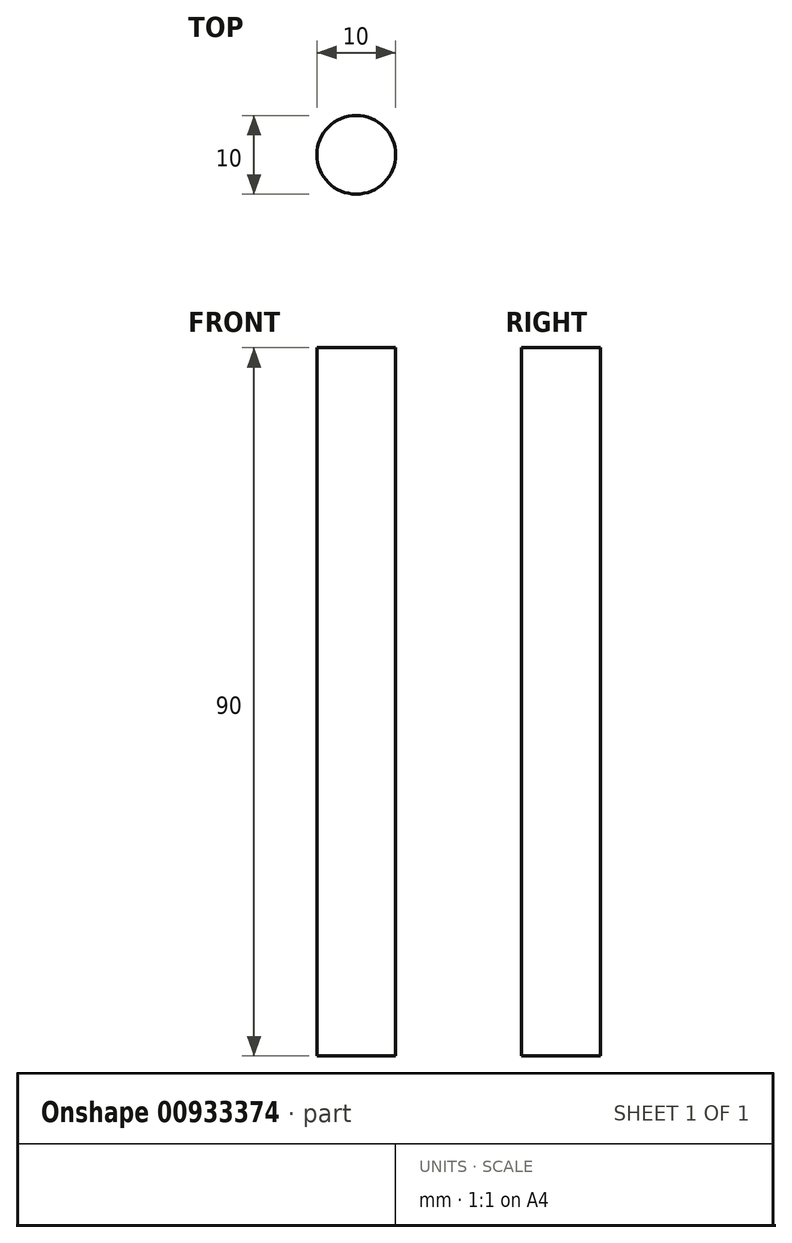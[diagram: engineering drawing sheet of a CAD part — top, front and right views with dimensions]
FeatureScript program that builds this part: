
annotation { "Feature Type Name" : "Feature", "Feature Type Description" : "" }
export const myFeature = defineFeature(function(context is Context, id is Id, definition is map)
    precondition{}
    {
        {
            var Q0;
            Q0=qCreatedBy(makeId("Top.planeOp"),FACE);
            var sketch = newSketch(context, id + "F0", { "sketchPlane" : qUnion([Q0])});
            skCircle(sketch, "E0", {"center": v(0, 0) * mm, "radius": 5 * mm});
            skSolve(sketch);
        }
        {
            var Q0;
            Q0=makeQuery(id+"F0.imprint","IMPRINT",FACE,{"disambiguationData":[TD([[makeQuery(id+"F0.imprint","IMPRINT",EDGE,{"derivedFrom":sQuery(id+"F0.wireOp",EDGE,"E0")}),1.0]])]});
            extrude(context, id + "F1", {"entities" : qUnion([Q0]), "depth" : 90 * mm, "offsetDistance" : 25 * mm});
        }
    });
